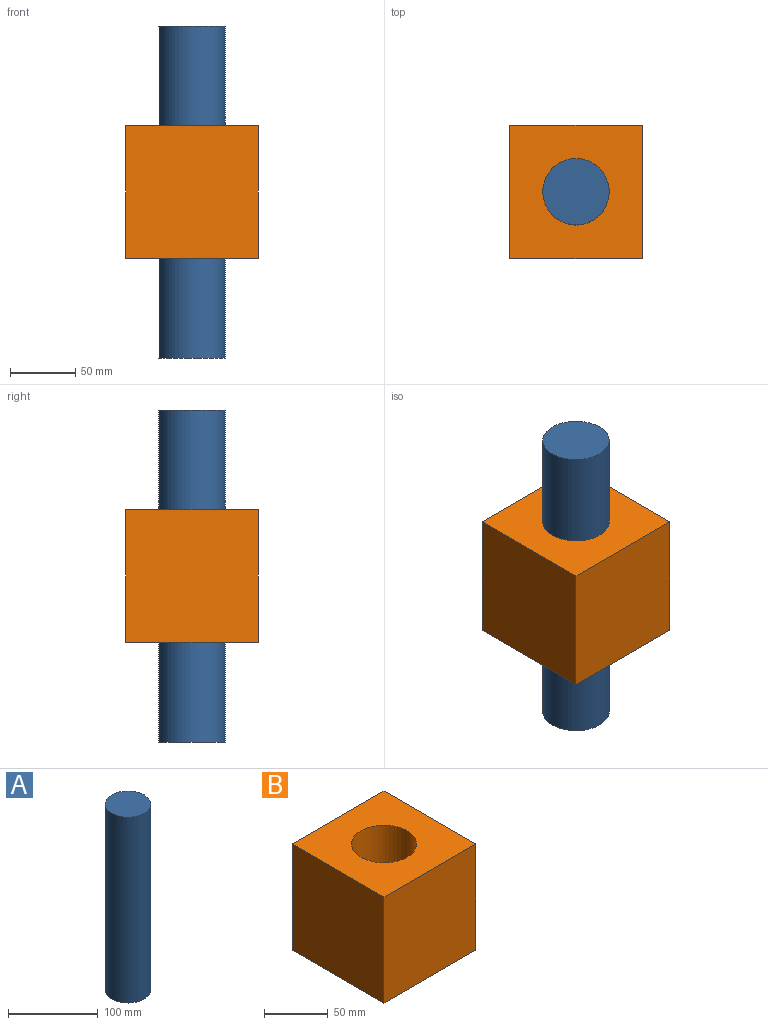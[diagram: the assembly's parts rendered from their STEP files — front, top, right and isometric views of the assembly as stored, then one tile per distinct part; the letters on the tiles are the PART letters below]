
ASSEMBLY  parts=2 mates=1
PART A: 3 faces, bbox 50.8x50.8x254 mm
  f0: cylinder r=25.4mm len=254mm, axis (0,0,-1), area 40536.6mm2, adj f1,f2
  f1: plane 50.8x50.8mm, normal (0,0,1), area 2026.8mm2, adj f0
  f2: plane 50.8x50.8mm, normal (0,0,-1), area 2026.8mm2, adj f0
PART B: 7 faces, bbox 101.6x101.6x101.6 mm
  f0: plane 101.6x101.6mm, normal (1,0,0), area 10322.6mm2, adj f1,f3,f5,f6
  f1: plane 101.6x101.6mm, normal (0,1,0), area 10322.6mm2, adj f0,f2,f5,f6
  f2: plane 101.6x101.6mm, normal (-1,0,0), area 10322.6mm2, adj f1,f3,f5,f6
  f3: plane 101.6x101.6mm, normal (0,-1,0), area 10322.6mm2, adj f0,f2,f5,f6
  f4: cylinder r=25.4mm len=101.6mm, axis (0,0,-1), area 16214.6mm2, adj f5,f6
  f5: plane 101.6x101.6mm, normal (0,0,1), area 8295.7mm2, adj f0,f1,f2,f3,f4
  f6: plane 101.6x101.6mm, normal (0,0,-1), area 8295.7mm2, adj f0,f1,f2,f3,f4
PLACE A t=(-109.7,-122.85,-72.51)mm
PLACE B t=(-109.7,-122.85,3.69)mm
MATE cylindrical A.f0 <-> B.f4  axis (0,0,-1) through (-109.7,-122.85,54.49)mm
